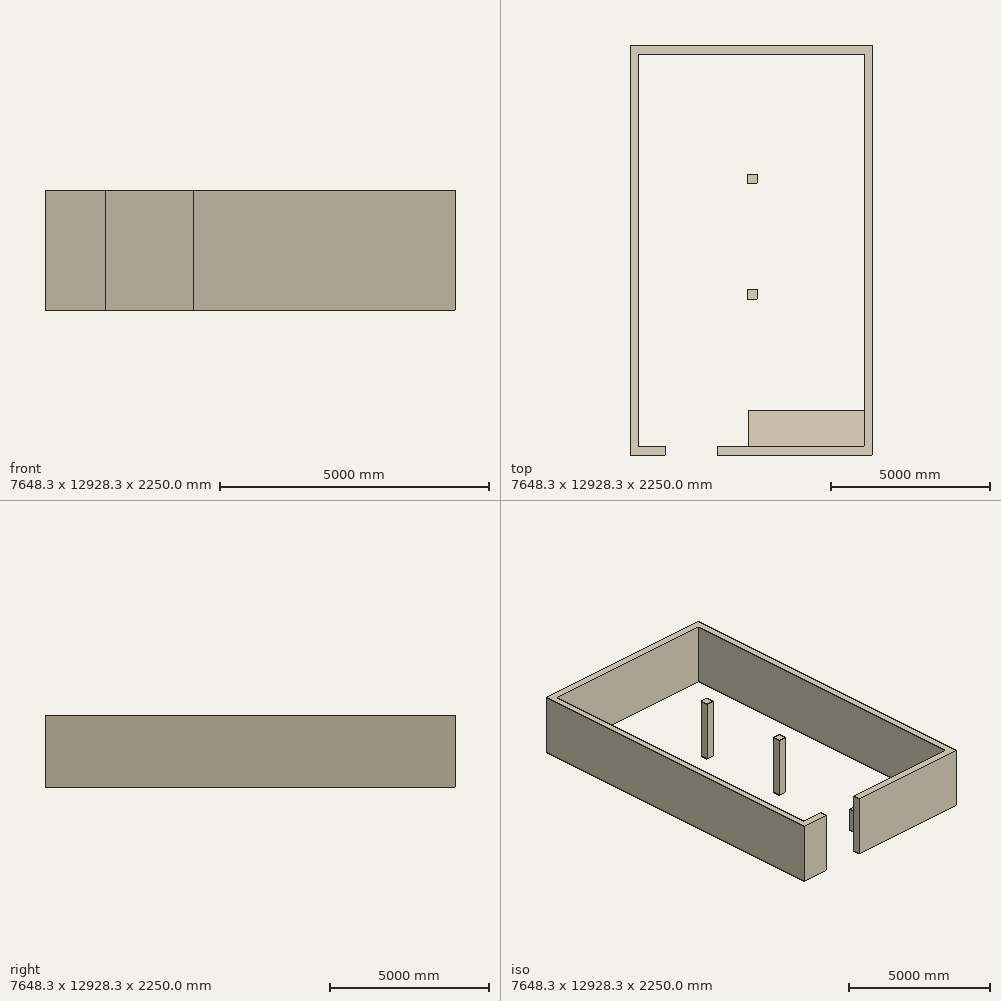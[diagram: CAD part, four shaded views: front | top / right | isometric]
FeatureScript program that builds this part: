
annotation { "Feature Type Name" : "Feature", "Feature Type Description" : "" }
export const myFeature = defineFeature(function(context is Context, id is Id, definition is map)
    precondition{}
    {
        {
            var Q0;
            Q0=qCreatedBy(makeId("Top.planeOp"),FACE);
            var sketch = newSketch(context, id + "F0", { "sketchPlane" : qUnion([Q0])});
            skLineSegment(sketch, "E0.bottom", {"start": v(3550, -6190) * mm, "end": v(-3550, -6190) * mm});
            skLineSegment(sketch, "E0.top", {"start": v(3550, 6190) * mm, "end": v(-3550, 6190) * mm});
            skLineSegment(sketch, "E0.left", {"start": v(3550, -6190) * mm, "end": v(3550, 6190) * mm});
            skLineSegment(sketch, "E0.right", {"start": v(-3550, -6190) * mm, "end": v(-3550, 6190) * mm});
            skPoint(sketch, "E0.middle", {"position": v(0, 0) * mm});
            skLineSegment(sketch, "E1.bottom", {"start": v(-3550, -6190) * mm, "end": v(-2710, -6190) * mm});
            skLineSegment(sketch, "E1.top", {"start": v(-3550, -1540) * mm, "end": v(-120, -1540) * mm, "construction": true});
            skLineSegment(sketch, "E1.left", {"start": v(-3550, -6190) * mm, "end": v(-3550, -1540) * mm});
            skLineSegment(sketch, "E1.right", {"start": v(-120, -6190) * mm, "end": v(-120, -1540) * mm, "construction": true});
            skLineSegment(sketch, "E2.bottom", {"start": v(-120, -1540) * mm, "end": v(185, -1540) * mm});
            skLineSegment(sketch, "E2.top", {"start": v(-120, -1235) * mm, "end": v(185, -1235) * mm});
            skLineSegment(sketch, "E2.left", {"start": v(-120, -1540) * mm, "end": v(-120, -1235) * mm});
            skLineSegment(sketch, "E2.right", {"start": v(185, -1540) * mm, "end": v(185, -1235) * mm});
            skLineSegment(sketch, "E3", {"start": v(32.5, -1235) * mm, "end": v(32.5, 2255) * mm, "construction": true});
            skPoint(sketch, "E3.endSnap0", {"position": v(32.5, -1235) * mm});
            skLineSegment(sketch, "E4.bottom", {"start": v(185, 2102.5) * mm, "end": v(-120, 2102.5) * mm});
            skLineSegment(sketch, "E4.top", {"start": v(185, 2407.5) * mm, "end": v(-120, 2407.5) * mm});
            skLineSegment(sketch, "E4.left", {"start": v(185, 2102.5) * mm, "end": v(185, 2407.5) * mm});
            skLineSegment(sketch, "E4.right", {"start": v(-120, 2102.5) * mm, "end": v(-120, 2407.5) * mm});
            skPoint(sketch, "E4.middle", {"position": v(32.5, 2255) * mm});
            skLineSegment(sketch, "E5.bottom", {"start": v(3550, -6190) * mm, "end": v(-100, -6190) * mm});
            skLineSegment(sketch, "E5.top", {"start": v(3550, -5040) * mm, "end": v(-100, -5040) * mm});
            skLineSegment(sketch, "E5.left", {"start": v(3550, -6190) * mm, "end": v(3550, -5040) * mm});
            skLineSegment(sketch, "E5.right", {"start": v(-100, -6190) * mm, "end": v(-100, -5040) * mm});
            skLineSegment(sketch, "E6", {"start": v(-2710, -6190) * mm, "end": v(-120, -6190) * mm});
            skLineSegment(sketch, "E7.bottom", {"start": v(-2710, -6190) * mm, "end": v(-1060, -6190) * mm});
            skLineSegment(sketch, "E8.bottom", {"start": v(-3550, 6190) * mm, "end": v(-3824.17, 6190) * mm});
            skLineSegment(sketch, "E8.top", {"start": v(-3550, -6190) * mm, "end": v(-3824.17, -6190) * mm});
            skLineSegment(sketch, "E8.left", {"start": v(-3550, 6190) * mm, "end": v(-3550, -6190) * mm});
            skLineSegment(sketch, "E8.right", {"start": v(-3824.17, 6190) * mm, "end": v(-3824.17, -6190) * mm});
            skLineSegment(sketch, "E9.bottom", {"start": v(-3824.17, 6190) * mm, "end": v(3550, 6190) * mm});
            skLineSegment(sketch, "E9.top", {"start": v(-3824.17, 6464.17) * mm, "end": v(3550, 6464.17) * mm});
            skLineSegment(sketch, "E9.left", {"start": v(-3824.17, 6190) * mm, "end": v(-3824.17, 6464.17) * mm});
            skLineSegment(sketch, "E9.right", {"start": v(3550, 6190) * mm, "end": v(3550, 6464.17) * mm});
            skLineSegment(sketch, "E10.bottom", {"start": v(3550, 6464.17) * mm, "end": v(3824.17, 6464.17) * mm});
            skLineSegment(sketch, "E10.top", {"start": v(3550, -6190) * mm, "end": v(3824.17, -6190) * mm});
            skLineSegment(sketch, "E10.left", {"start": v(3550, 6464.17) * mm, "end": v(3550, -6190) * mm});
            skLineSegment(sketch, "E10.right", {"start": v(3824.17, 6464.17) * mm, "end": v(3824.17, -6190) * mm});
            skLineSegment(sketch, "E11.bottom", {"start": v(3824.17, -6190) * mm, "end": v(-1060, -6190) * mm});
            skLineSegment(sketch, "E11.top", {"start": v(3824.17, -6464.17) * mm, "end": v(-1060, -6464.17) * mm});
            skLineSegment(sketch, "E11.left", {"start": v(3824.17, -6190) * mm, "end": v(3824.17, -6464.17) * mm});
            skLineSegment(sketch, "E11.right", {"start": v(-1060, -6190) * mm, "end": v(-1060, -6464.17) * mm});
            skLineSegment(sketch, "E12.bottom", {"start": v(-3824.17, -6190) * mm, "end": v(-2710, -6190) * mm});
            skLineSegment(sketch, "E12.top", {"start": v(-3824.17, -6464.17) * mm, "end": v(-2710, -6464.17) * mm});
            skLineSegment(sketch, "E12.left", {"start": v(-3824.17, -6190) * mm, "end": v(-3824.17, -6464.17) * mm});
            skLineSegment(sketch, "E12.right", {"start": v(-2710, -6190) * mm, "end": v(-2710, -6464.17) * mm});
            skSolve(sketch);
        }
        {
            var Q0;
            {var subQ3=sQuery(id+"F0.wireOp",EDGE,"E8.right");Q0=makeQuery(id+"F0.imprint","IMPRINT",FACE,{"disambiguationData":[TD([[makeQuery(id+"F0.imprint","IMPRINT",EDGE,{"derivedFrom":subQ3}),1.0]])]});}
            var Q1;
            {var subQ1=sQuery(id+"F0.wireOp",EDGE,"E9.top");Q1=makeQuery(id+"F0.imprint","IMPRINT",FACE,{"disambiguationData":[TD([[makeQuery(id+"F0.imprint","IMPRINT",EDGE,{"derivedFrom":subQ1}),-1.0]])]});}
            var Q2;
            {var subQ5=sQuery(id+"F0.wireOp",EDGE,"E10.bottom");Q2=makeQuery(id+"F0.imprint","IMPRINT",FACE,{"disambiguationData":[TD([[makeQuery(id+"F0.imprint","IMPRINT",EDGE,{"derivedFrom":subQ5}),-1.0]])]});}
            var Q3;
            Q3=makeQuery(id+"F0.imprint","IMPRINT",FACE,{"disambiguationData":[TD([[makeQuery(id+"F0.imprint","IMPRINT",EDGE,{"derivedFrom":sQuery(id+"F0.wireOp",EDGE,"E11.top")}),-1.0]])]});
            var Q4;
            Q4=makeQuery(id+"F0.imprint","IMPRINT",FACE,{"disambiguationData":[TD([[makeQuery(id+"F0.imprint","IMPRINT",EDGE,{"derivedFrom":sQuery(id+"F0.wireOp",EDGE,"E12.top")}),1.0]])]});
            var Q5;
            Q5=makeQuery(id+"F0.imprint","IMPRINT",FACE,{"disambiguationData":[TD([[makeQuery(id+"F0.imprint","IMPRINT",EDGE,{"derivedFrom":sQuery(id+"F0.wireOp",EDGE,"E2.bottom")}),1.0]])]});
            var Q6;
            Q6=makeQuery(id+"F0.imprint","IMPRINT",FACE,{"disambiguationData":[TD([[makeQuery(id+"F0.imprint","IMPRINT",EDGE,{"derivedFrom":sQuery(id+"F0.wireOp",EDGE,"E4.bottom")}),-1.0]])]});
            extrude(context, id + "F1", {"entities" : qUnion([Q0, Q1, Q2, Q3, Q4, Q5, Q6]), "depth" : 2250 * mm, "offsetDistance" : 25 * mm});
        }
        {
            var Q0;
            {var subQ0=sQuery(id+"F0.wireOp",EDGE,"E5.top");Q0=makeQuery(id+"F0.imprint","IMPRINT",FACE,{"disambiguationData":[TD([[makeQuery(id+"F0.imprint","IMPRINT",EDGE,{"derivedFrom":subQ0}),1.0]])]});}
            extrude(context, id + "F2", {"entities" : qUnion([Q0]), "depth" : 850 * mm, "offsetDistance" : 25 * mm});
        }
        {
            var Q0;
            Q0=makeQuery(id+"F1.opExtrude","SWEPT_EDGE",EDGE,{"disambiguationData":[OSD([sQuery(id+"F0.wireOp",EDGE,"E2.top"),sQuery(id+"F0.wireOp",EDGE,"E2.left")])]});
            var Q1;
            Q1=makeQuery(id+"F1.opExtrude","SWEPT_EDGE",EDGE,{"disambiguationData":[OSD([sQuery(id+"F0.wireOp",EDGE,"E2.top"),sQuery(id+"F0.wireOp",EDGE,"E2.right")])]});
            var Q2;
            Q2=makeQuery(id+"F1.opExtrude","SWEPT_EDGE",EDGE,{"disambiguationData":[OSD([sQuery(id+"F0.wireOp",EDGE,"E2.bottom"),sQuery(id+"F0.wireOp",EDGE,"E2.left")])]});
            var Q3;
            Q3=makeQuery(id+"F1.opExtrude","SWEPT_FACE",FACE,{"disambiguationData":[OSD([sQuery(id+"F0.wireOp",EDGE,"E4.right")])]});
            var Q4;
            Q4=makeQuery(id+"F1.opExtrude","SWEPT_FACE",FACE,{"disambiguationData":[OSD([sQuery(id+"F0.wireOp",EDGE,"E4.top")])]});
            var Q5;
            Q5=makeQuery(id+"F1.opExtrude","SWEPT_FACE",FACE,{"disambiguationData":[OSD([sQuery(id+"F0.wireOp",EDGE,"E2.top")])]});
            var Q6;
            Q6=makeQuery(id+"F1.opExtrude","SWEPT_FACE",FACE,{"disambiguationData":[OSD([sQuery(id+"F0.wireOp",EDGE,"E2.left")])]});
            var Q7;
            Q7=makeQuery(id+"F1.opExtrude","SWEPT_FACE",FACE,{"disambiguationData":[OSD([sQuery(id+"F0.wireOp",EDGE,"E2.bottom")])]});
            var Q8;
            Q8=makeQuery(id+"F1.opExtrude","SWEPT_EDGE",EDGE,{"disambiguationData":[OSD([sQuery(id+"F0.wireOp",EDGE,"E4.bottom"),sQuery(id+"F0.wireOp",EDGE,"E4.right")])]});
            var Q9;
            Q9=makeQuery(id+"F1.opExtrude","SWEPT_FACE",FACE,{"disambiguationData":[OSD([sQuery(id+"F0.wireOp",EDGE,"E4.bottom")])]});
            var Q10;
            Q10=makeQuery(id+"F1.opExtrude","SWEPT_FACE",FACE,{"disambiguationData":[OSD([sQuery(id+"F0.wireOp",EDGE,"E2.right")])]});
            var Q11;
            Q11=makeQuery(id+"F1.opExtrude","SWEPT_FACE",FACE,{"disambiguationData":[OSD([sQuery(id+"F0.wireOp",EDGE,"E4.left")])]});
            fillet(context, id + "F3", {"entities" : qUnion([Q0, Q1, Q2, Q3, Q4, Q5, Q6, Q7, Q8, Q9, Q10, Q11]), "radius" : 6.35 * mm, "tangentPropagation" : true, "allowEdgeOverflow" : false});
        }
    });
